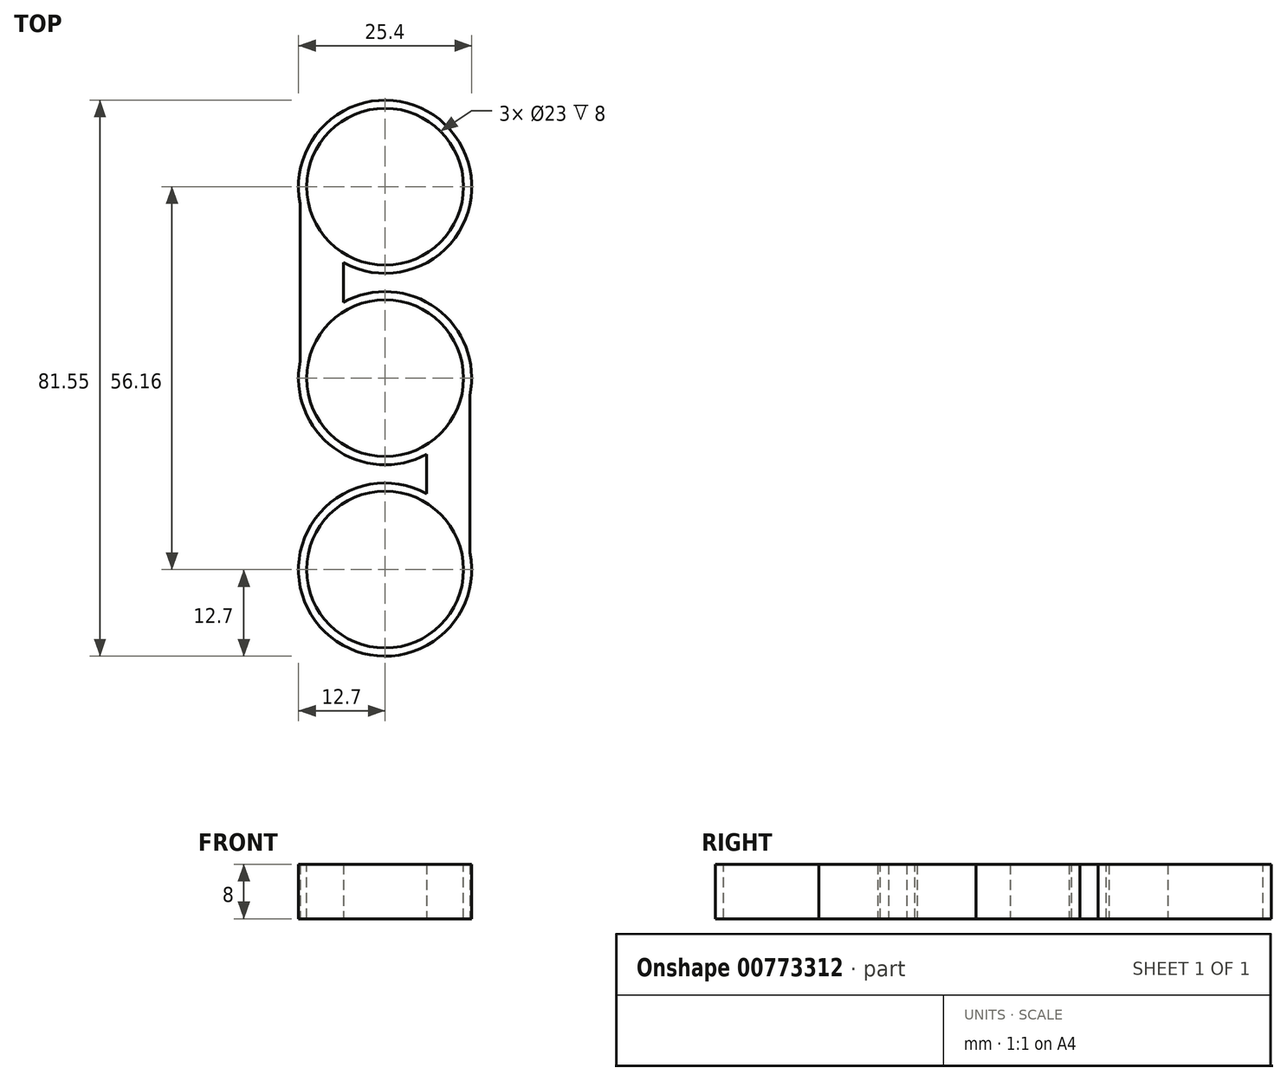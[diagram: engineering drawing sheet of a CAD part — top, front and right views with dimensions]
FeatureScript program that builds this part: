
annotation { "Feature Type Name" : "Feature", "Feature Type Description" : "" }
export const myFeature = defineFeature(function(context is Context, id is Id, definition is map)
    precondition{}
    {
        {
            var Q0;
            Q0=qCreatedBy(makeId("Top.planeOp"),FACE);
            var sketch = newSketch(context, id + "F0", { "sketchPlane" : qUnion([Q0])});
            skCircle(sketch, "E0", {"center": v(0, 0) * mm, "radius": 11.5 * mm});
            skCircle(sketch, "E1", {"center": v(0, 28.08) * mm, "radius": 11.5 * mm});
            skCircle(sketch, "E2", {"center": v(0, -28.08) * mm, "radius": 11.5 * mm});
            skSolve(sketch);
        }
        {
            var Q0;
            Q0=qCreatedBy(makeId("Top.planeOp"),FACE);
            var sketch = newSketch(context, id + "F1", { "sketchPlane" : qUnion([Q0])});
            skLineSegment(sketch, "E3.bottom", {"start": v(-12.45, 28.1) * mm, "end": v(-6.1, 28.1) * mm});
            skLineSegment(sketch, "E3.top", {"start": v(-12.45, 0) * mm, "end": v(-6.1, 0) * mm});
            skLineSegment(sketch, "E3.left", {"start": v(-12.45, 28.1) * mm, "end": v(-12.45, 0) * mm});
            skLineSegment(sketch, "E3.right", {"start": v(-6.1, 28.1) * mm, "end": v(-6.1, 0) * mm});
            skLineSegment(sketch, "E4.bottom", {"start": v(6.1, 0) * mm, "end": v(12.45, 0) * mm});
            skLineSegment(sketch, "E4.top", {"start": v(6.1, -28.1) * mm, "end": v(12.45, -28.1) * mm});
            skLineSegment(sketch, "E4.left", {"start": v(6.1, 0) * mm, "end": v(6.1, -28.1) * mm});
            skLineSegment(sketch, "E4.right", {"start": v(12.45, 0) * mm, "end": v(12.45, -28.1) * mm});
            skCircle(sketch, "E5", {"center": v(0, 28.07) * mm, "radius": 12.7 * mm});
            skCircle(sketch, "E6", {"center": v(0, 0) * mm, "radius": 12.7 * mm});
            skCircle(sketch, "E7", {"center": v(0, -28.08) * mm, "radius": 12.7 * mm});
            skSolve(sketch);
        }
        {
            var Q0;
            Q0 = qSketchRegion(id + "F1", true);
            extrude(context, id + "F2", {"entities" : qUnion([Q0]), "endBound" : BoundingType.SYMMETRIC, "depth" : 8 * mm, "offsetDistance" : 25.4 * mm});
        }
        {
            var Q0;
            Q0 = qSketchRegion(id + "F0", true);
            extrude(context, id + "F3", {"entities" : qUnion([Q0]), "operationType" : NewBodyOperationType.REMOVE, "endBound" : BoundingType.SYMMETRIC, "oppositeDirection" : true, "depth" : 8 * mm, "offsetDistance" : 25.4 * mm});
        }
    });
